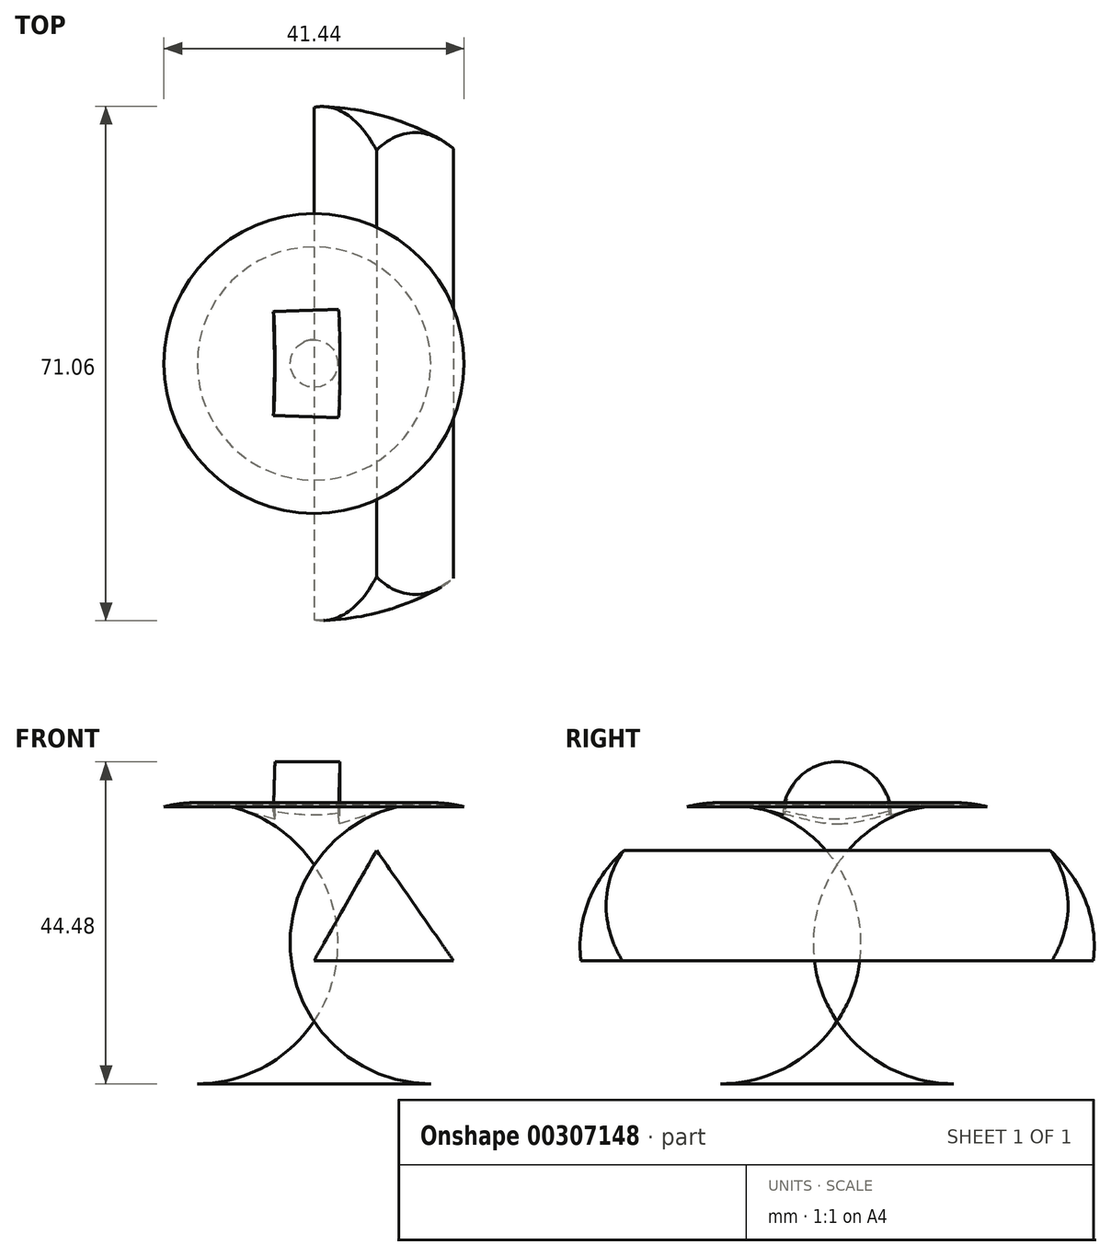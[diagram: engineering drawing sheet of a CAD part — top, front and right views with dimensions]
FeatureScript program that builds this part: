
annotation { "Feature Type Name" : "Feature", "Feature Type Description" : "" }
export const myFeature = defineFeature(function(context is Context, id is Id, definition is map)
    precondition{}
    {
        {
            var Q0;
            Q0=qCreatedBy(makeId("Front.planeOp"),FACE);
            var sketch = newSketch(context, id + "F0", { "sketchPlane" : qUnion([Q0])});
            skLineSegment(sketch, "E0", {"start": v(0, 79.15) * mm, "end": v(0, -79.43) * mm});
            skSolve(sketch);
        }
        {
            var Q0;
            Q0=qCreatedBy(makeId("Front.planeOp"),FACE);
            var sketch = newSketch(context, id + "F1", { "sketchPlane" : qUnion([Q0])});
            skLineSegment(sketch, "E1", {"start": v(0, 0) * mm, "end": v(16.12, 0) * mm});
            skArc(sketch, "E2", {"start": v(16.12, 0) * mm, "mid": v(35.4, 17.1) * mm, "end": v(20.72, 38.28) * mm});
            skFitSpline(sketch, "E3", {"points": [v(20.72, 38.28) * mm, v(12.38, 38.28) * mm, v(3.74, 35.98) * mm, v(0, 34.82) * mm], "startDerivative": vector(-22.07, 1.73) * mm, "endDerivative": vector(-13.17, -3.92) * mm});
            skLineSegment(sketch, "E4", {"start": v(0, 34.82) * mm, "end": v(0, 0) * mm});
            skSolve(sketch);
        }
        {
            var Q0;
            Q0 = qSketchRegion(id + "F1", true);
            var Q1;
            Q1=sQuery(id+"F0.wireOp",EDGE,"E0");
            revolve(context, id + "F2", {"entities" : qUnion([Q0]), "axis" : qUnion([Q1]), "revolveType" : RevolveType.FULL});
        }
        {
            var Q0;
            Q0=qCreatedBy(makeId("Front.planeOp"),FACE);
            var sketch = newSketch(context, id + "F3", { "sketchPlane" : qUnion([Q0])});
            skLineSegment(sketch, "E5", {"start": v(-5.4, 37.3) * mm, "end": v(-5.4, 44.48) * mm});
            skLineSegment(sketch, "E6", {"start": v(-5.4, 44.48) * mm, "end": v(3.6, 44.48) * mm});
            skLineSegment(sketch, "E7", {"start": v(3.6, 44.48) * mm, "end": v(3.6, 37) * mm});
            skLineSegment(sketch, "E8", {"start": v(3.6, 37) * mm, "end": v(-5.4, 37.3) * mm});
            skSolve(sketch);
        }
        {
            var Q0;
            Q0 = qSketchRegion(id + "F3", true);
            var Q1;
            Q1=sQuery(id+"F3.wireOp",EDGE,"E8");
            revolve(context, id + "F4", {"operationType" : NewBodyOperationType.ADD, "entities" : qUnion([Q0]), "axis" : qUnion([Q1]), "revolveType" : RevolveType.FULL});
        }
        {
            var Q0;
            Q0=qCreatedBy(makeId("Front.planeOp"),FACE);
            var sketch = newSketch(context, id + "F5", { "sketchPlane" : qUnion([Q0])});
            skLineSegment(sketch, "E9", {"start": v(-20.15, 25.33) * mm, "end": v(-16.12, 31.66) * mm});
            skLineSegment(sketch, "E10", {"start": v(-12.09, 25.33) * mm, "end": v(-16.12, 31.66) * mm});
            skLineSegment(sketch, "E11", {"start": v(-12.09, 25.33) * mm, "end": v(-20.15, 25.33) * mm});
            skLineSegment(sketch, "E12", {"start": v(8.63, 32.23) * mm, "end": v(0, 16.98) * mm});
            skLineSegment(sketch, "E13", {"start": v(0, 16.98) * mm, "end": v(19.28, 16.98) * mm});
            skLineSegment(sketch, "E14", {"start": v(19.28, 16.98) * mm, "end": v(8.63, 32.23) * mm});
            skSolve(sketch);
        }
        {
            var Q0;
            Q0 = qSketchRegion(id + "F5", true);
            extrude(context, id + "F6", {"entities" : qUnion([Q0]), "operationType" : NewBodyOperationType.REMOVE, "endBound" : BoundingType.SYMMETRIC, "oppositeDirection" : true, "depth" : 152.4 * mm});
        }
        {
            var Q0;
            Q0=qCreatedBy(makeId("Front.planeOp"),FACE);
            var sketch = newSketch(context, id + "F7", { "sketchPlane" : qUnion([Q0])});
            skFitSpline(sketch, "E15", {"points": [v(-23.02, 13.53) * mm, v(-19.28, 8.35) * mm, v(-16.4, 11.22) * mm, v(-9.5, 6.9) * mm, v(-5.18, 12.09) * mm, v(0, 6.9) * mm, v(6.9, 10.94) * mm, v(10.36, 6.33) * mm, v(14.97, 10.36) * mm, v(19.28, 6.62) * mm, v(21.59, 10.94) * mm, v(20.43, 2.88) * mm, v(14.97, 6.33) * mm, v(9.5, 2.6) * mm, v(7.2, 6.33) * mm, v(0, 3.74) * mm, v(-4.32, 6.62) * mm, v(-11.8, 3.45) * mm, v(-15.83, 6.04) * mm, v(-20.43, 4.6) * mm, v(-23.02, 13.53) * mm]});
            skSolve(sketch);
        }
        {
            var Q0;
            Q0 = qSketchRegion(id + "F7", true);
            extrude(context, id + "F8", {"entities" : qUnion([Q0]), "operationType" : NewBodyOperationType.REMOVE, "endBound" : BoundingType.SYMMETRIC, "oppositeDirection" : true, "depth" : 152.4 * mm});
        }
    });
